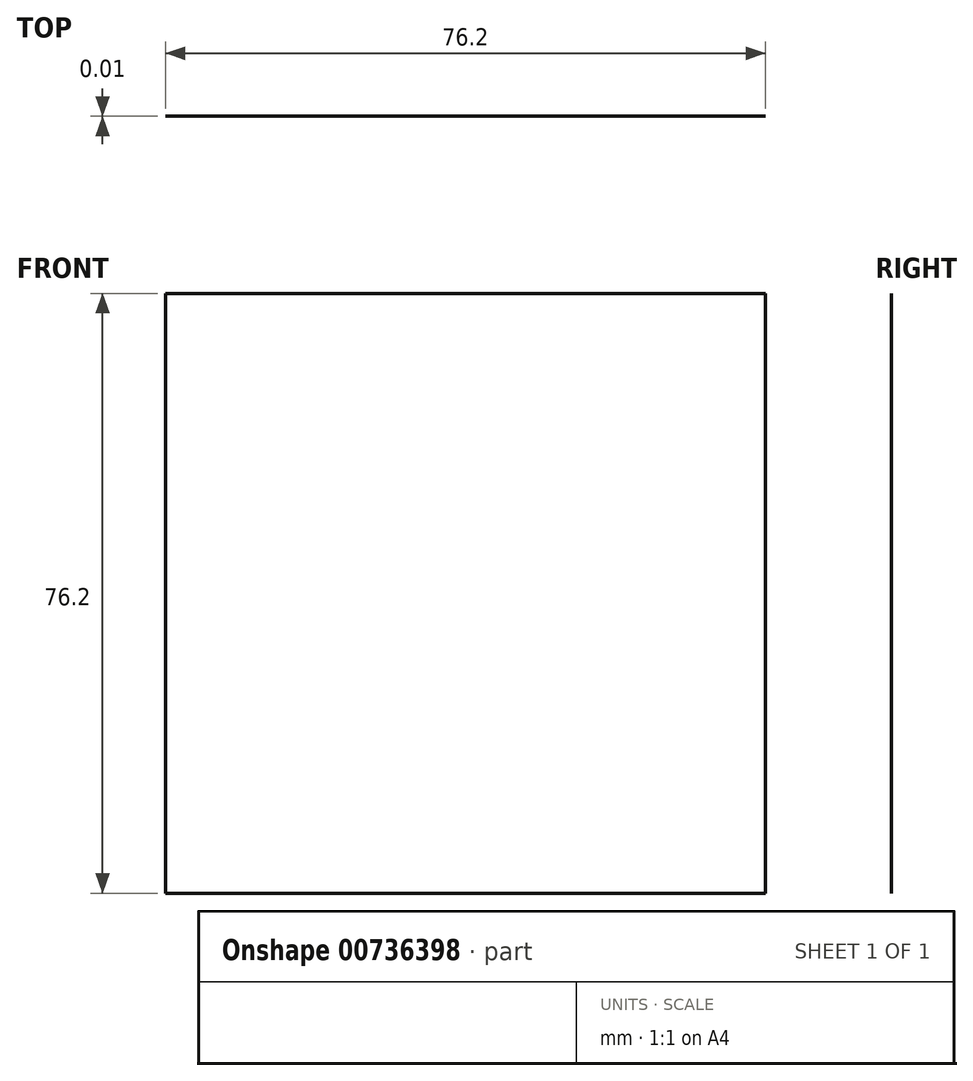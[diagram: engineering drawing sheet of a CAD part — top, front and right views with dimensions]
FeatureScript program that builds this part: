
annotation { "Feature Type Name" : "Feature", "Feature Type Description" : "" }
export const myFeature = defineFeature(function(context is Context, id is Id, definition is map)
    precondition{}
    {
        {
            var Q0;
            Q0=qCreatedBy(makeId("Front.planeOp"),FACE);
            var sketch = newSketch(context, id + "F0", { "sketchPlane" : qUnion([Q0])});
            skLineSegment(sketch, "E0.bottom", {"start": v(0, 0) * mm, "end": v(76.2, 0) * mm});
            skLineSegment(sketch, "E0.top", {"start": v(0, 76.2) * mm, "end": v(76.2, 76.2) * mm});
            skLineSegment(sketch, "E0.left", {"start": v(0, 0) * mm, "end": v(0, 76.2) * mm});
            skLineSegment(sketch, "E0.right", {"start": v(76.2, 0) * mm, "end": v(76.2, 76.2) * mm});
            skSolve(sketch);
        }
        {
            var Q0;
            Q0=makeQuery(id+"F0.imprint","IMPRINT",FACE,{"disambiguationData":[TD([[makeQuery(id+"F0.imprint","IMPRINT",EDGE,{"derivedFrom":sQuery(id+"F0.wireOp",EDGE,"E0.bottom")}),1.0]])]});
            extrude(context, id + "F1", {"entities" : qUnion([Q0]), "depth" : 3 / 406.4 * mm, "offsetDistance" : 25.4 * mm});
        }
    });
